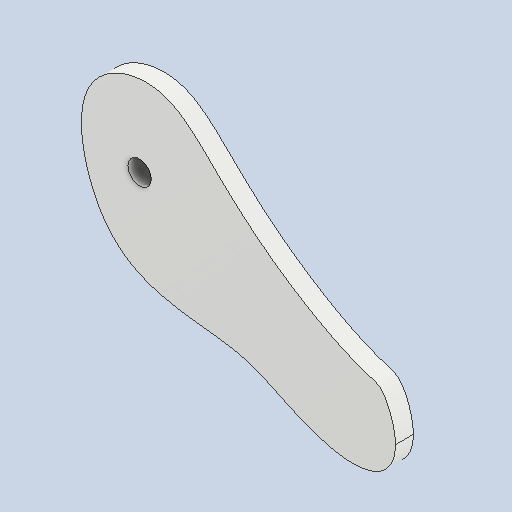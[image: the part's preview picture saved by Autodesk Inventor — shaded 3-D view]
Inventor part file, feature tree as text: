
AUTODESK INVENTOR PART (.ipt)
format: ipt  version: 2022 (Build 260153000, 153)  size: 108,032 bytes
history: native  units: in
note: dims shown in document units (in); Inventor stores cm internally (conversion verified against a paired STEP export)
features: other x3, sketch x1
ambient origin geometry x8: Origin, YZ Plane, XZ Plane, XY Plane, X Axis, Y Axis, Z Axis, Center Point
bodies: Solid1 (feature_tree)
feature tree (4):
  other  "Component34.ipt"
  other  "Solid1::Component34.ipt"
  other  "TaggingFeature1"
  sketch  "Sketch2"  dims[d0=0.3937in]
